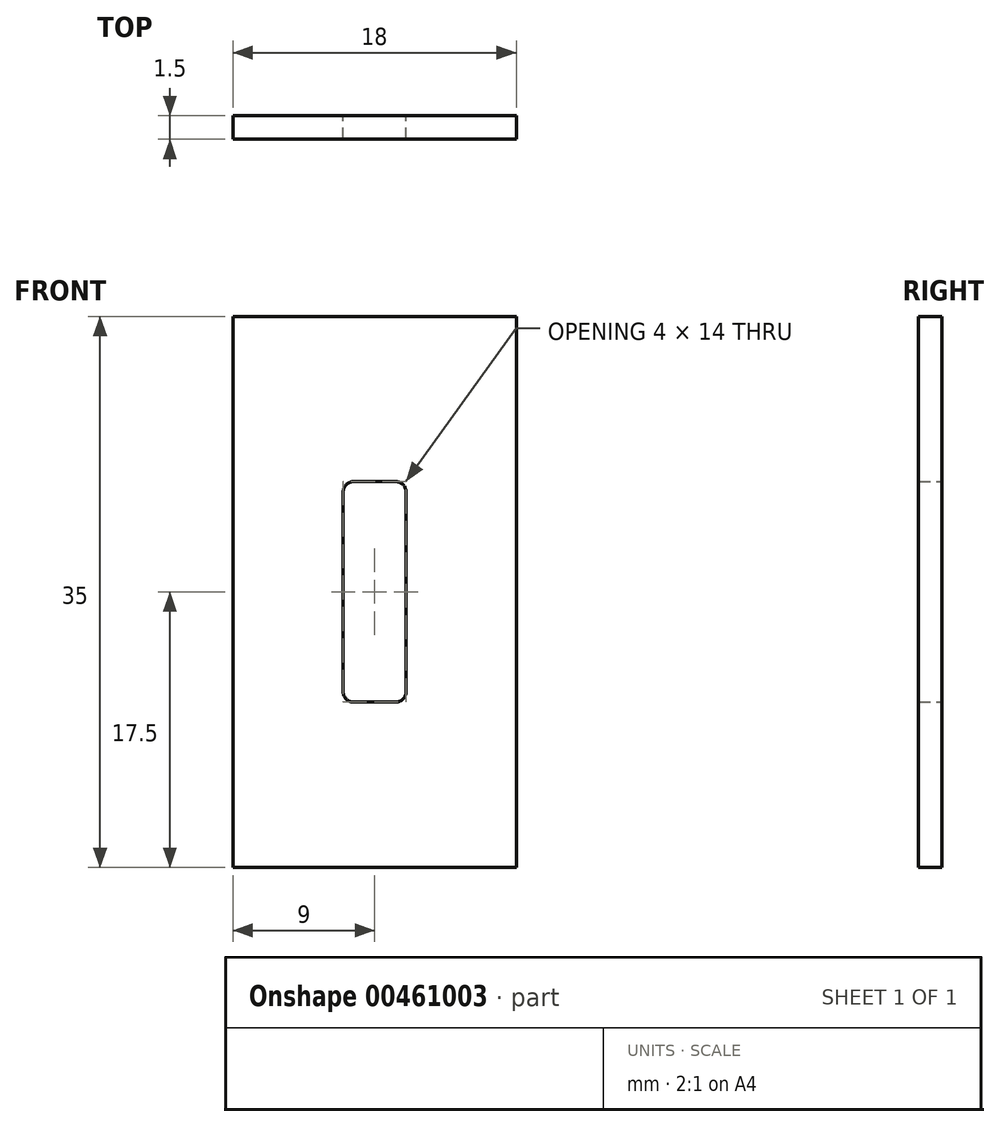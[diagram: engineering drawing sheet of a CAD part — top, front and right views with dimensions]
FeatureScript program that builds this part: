
annotation { "Feature Type Name" : "Feature", "Feature Type Description" : "" }
export const myFeature = defineFeature(function(context is Context, id is Id, definition is map)
    precondition{}
    {
        {
            var Q0;
            Q0=qCreatedBy(makeId("Front.planeOp"),FACE);
            var sketch = newSketch(context, id + "F0", { "sketchPlane" : qUnion([Q0])});
            skLineSegment(sketch, "E0.bottom", {"start": v(9, 17.5) * mm, "end": v(-9, 17.5) * mm});
            skLineSegment(sketch, "E0.top", {"start": v(9, -17.5) * mm, "end": v(-9, -17.5) * mm});
            skLineSegment(sketch, "E0.left", {"start": v(9, 17.5) * mm, "end": v(9, -17.5) * mm});
            skLineSegment(sketch, "E0.right", {"start": v(-9, 17.5) * mm, "end": v(-9, -17.5) * mm});
            skPoint(sketch, "E0.middle", {"position": v(0, 0) * mm});
            skLineSegment(sketch, "E1.bottom", {"start": v(1.35, 7) * mm, "end": v(-1.35, 7) * mm});
            skLineSegment(sketch, "E1.top", {"start": v(1.35, -7) * mm, "end": v(-1.35, -7) * mm});
            skLineSegment(sketch, "E1.left", {"start": v(2, 6.35) * mm, "end": v(2, -6.35) * mm});
            skLineSegment(sketch, "E1.right", {"start": v(-2, 6.35) * mm, "end": v(-2, -6.35) * mm});
            skPoint(sketch, "E2.visualSharp", {"position": v(-2, 7) * mm});
            skArc(sketch, "E2.filletArc", {"start": v(-1.35, 7) * mm, "mid": v(-1.8, 6.8) * mm, "end": v(-2, 6.35) * mm});
            skPoint(sketch, "E3.visualSharp", {"position": v(2, 7) * mm});
            skArc(sketch, "E3.filletArc", {"start": v(2, 6.35) * mm, "mid": v(1.8, 6.8) * mm, "end": v(1.35, 7) * mm});
            skPoint(sketch, "E4.visualSharp", {"position": v(-2, -7) * mm});
            skArc(sketch, "E4.filletArc", {"start": v(-2, -6.35) * mm, "mid": v(-1.8, -6.8) * mm, "end": v(-1.35, -7) * mm});
            skPoint(sketch, "E5.visualSharp", {"position": v(2, -7) * mm});
            skArc(sketch, "E5.filletArc", {"start": v(1.35, -7) * mm, "mid": v(1.8, -6.8) * mm, "end": v(2, -6.35) * mm});
            skSolve(sketch);
        }
        {
            var Q0;
            Q0 = qSketchRegion(id + "F0", true);
            extrude(context, id + "F1", {"entities" : qUnion([Q0]), "depth" : 1.5 * mm});
        }
    });
